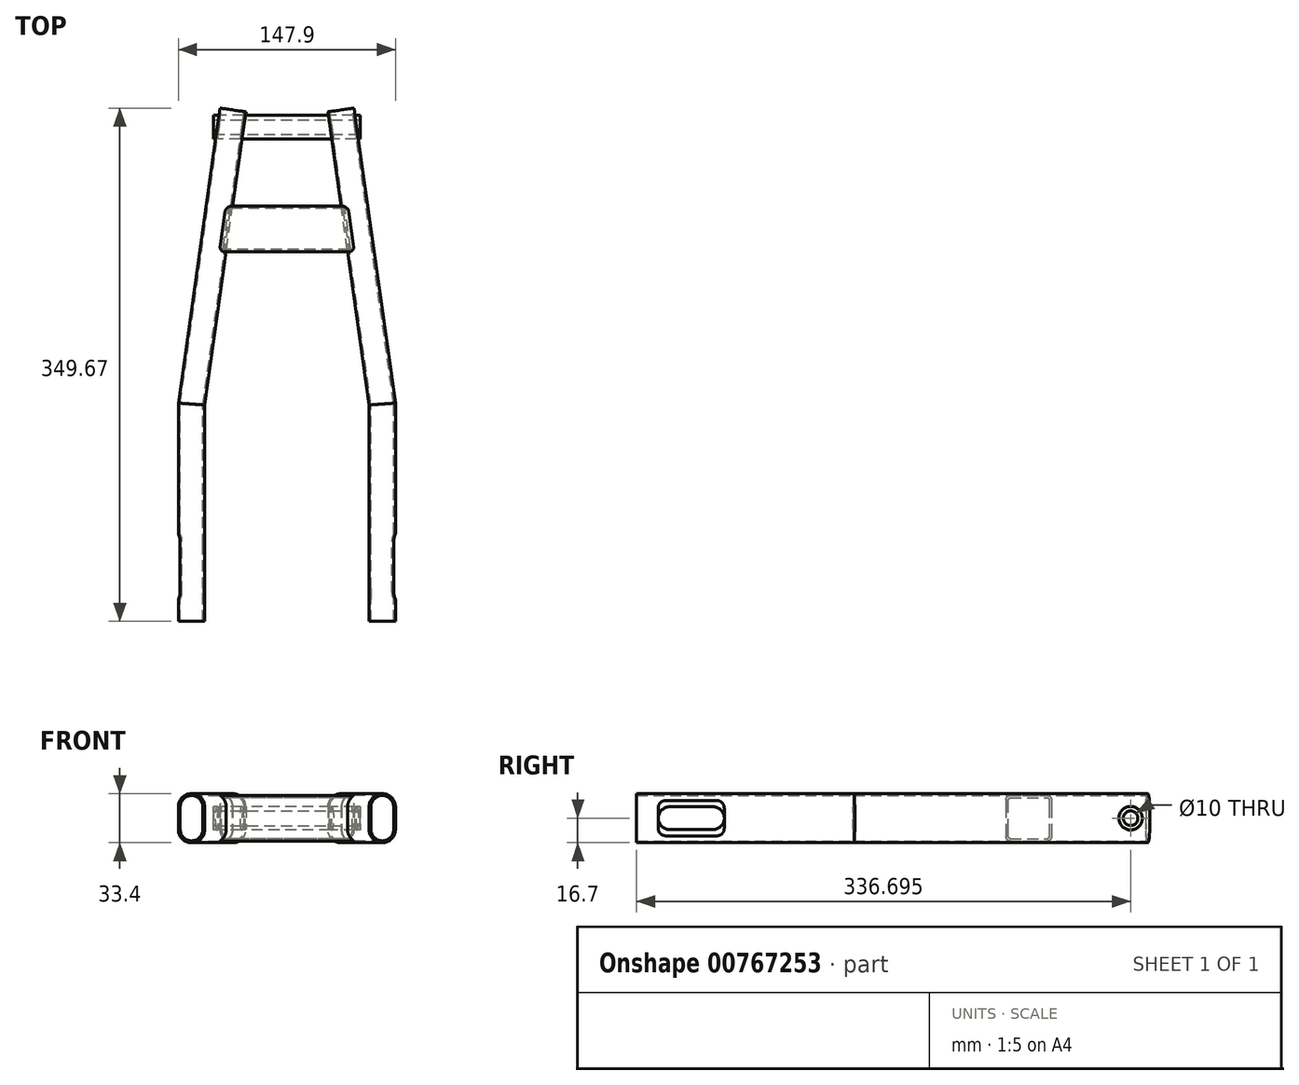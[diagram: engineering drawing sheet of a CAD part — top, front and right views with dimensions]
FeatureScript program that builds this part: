
annotation { "Feature Type Name" : "Feature", "Feature Type Description" : "" }
export const myFeature = defineFeature(function(context is Context, id is Id, definition is map)
    precondition{}
    {
        {
            var Q0;
            Q0=qCreatedBy(makeId("Top.planeOp"),FACE);
            var sketch = newSketch(context, id + "F0", { "sketchPlane" : qUnion([Q0])});
            skLineSegment(sketch, "E0", {"start": v(-65, 0) * mm, "end": v(-65, 148.03) * mm});
            skLineSegment(sketch, "E1", {"start": v(-65, 148.03) * mm, "end": v(-36.84, 348.42) * mm});
            skSolve(sketch);
        }
        {
            var Q0;
            Q0=qCreatedBy(makeId("Front.planeOp"),FACE);
            var sketch = newSketch(context, id + "F1", { "sketchPlane" : qUnion([Q0])});
            skLineSegment(sketch, "E2.left", {"start": v(-57.25, -7.75) * mm, "end": v(-57.25, 7.75) * mm});
            skLineSegment(sketch, "E2.right", {"start": v(-72.75, -7.75) * mm, "end": v(-72.75, 7.75) * mm});
            skPoint(sketch, "E2.middle", {"position": v(-65, 0) * mm});
            skArc(sketch, "E3", {"start": v(-57.25, 7.75) * mm, "mid": v(-65, 15.5) * mm, "end": v(-72.75, 7.75) * mm});
            skArc(sketch, "E4", {"start": v(-72.75, -7.75) * mm, "mid": v(-65, -15.5) * mm, "end": v(-57.25, -7.75) * mm});
            skCircle(sketch, "E5", {"center": v(-65, 0) * mm, "radius": 3 * mm});
            skLineSegment(sketch, "E6", {"start": v(-56.05, 7.75) * mm, "end": v(-56.05, -7.75) * mm});
            skLineSegment(sketch, "E7", {"start": v(-73.95, 7.75) * mm, "end": v(-73.95, -7.75) * mm});
            skArc(sketch, "E8", {"start": v(-56.05, 7.75) * mm, "mid": v(-65, 16.7) * mm, "end": v(-73.95, 7.75) * mm});
            skArc(sketch, "E9", {"start": v(-73.95, -7.75) * mm, "mid": v(-65, -16.7) * mm, "end": v(-56.05, -7.75) * mm});
            skSolve(sketch);
        }
        {
            var Q0;
            Q0 = qSketchRegion(id + "F1", true);
            var Q1;
            Q1=sQuery(id+"F0.wireOp",EDGE,"E0");
            var Q2;
            Q2=sQuery(id+"F0.wireOp",EDGE,"E1");
            sweep(context, id + "F2", {"profiles" : qUnion([Q0]), "path" : qUnion([Q1, Q2])});
        }
        {
            var Q0;
            Q0=makeQuery(id+"F2.opSweep","SWEPT_BODY",BODY,{"disambiguationData":[OSD([sQuery(id+"F0.wireOp",EDGE,"E1"),sQuery(id+"F1.wireOp",EDGE,"E2.left"),sQuery(id+"F1.wireOp",EDGE,"E2.right"),sQuery(id+"F1.wireOp",EDGE,"E3"),sQuery(id+"F1.wireOp",EDGE,"E4"),sQuery(id+"F1.wireOp",EDGE,"E6"),sQuery(id+"F1.wireOp",EDGE,"E7"),sQuery(id+"F1.wireOp",EDGE,"E8"),sQuery(id+"F1.wireOp",EDGE,"E9")])]});
            var Q1;
            Q1=qCreatedBy(makeId("Right.planeOp"),FACE);
            mirror(context, id + "F3", {"entities" : qUnion([Q0]), "mirrorPlane" : qUnion([Q1])});
        }
        {
            var Q0;
            Q0=makeQuery(id+"F3.opPattern","COPY",FACE,{"derivedFrom":makeQuery(id+"F2.opSweep","SWEPT_FACE",FACE,{"disambiguationData":[OSD([sQuery(id+"F0.wireOp",EDGE,"E0"),sQuery(id+"F1.wireOp",EDGE,"E7")])]}),"instanceName":"1"});
            cPlane(context, id + "F4", {"entities" : qUnion([Q0]), "cplaneType" : CPlaneType.OFFSET, "offset" : 25 * mm, "width" : 150 * mm, "height" : 150 * mm});
        }
        {
            var Q0;
            Q0=qCreatedBy(id+"F4.planeOp",FACE);
            var sketch = newSketch(context, id + "F5", { "sketchPlane" : qUnion([Q0])});
            skLineSegment(sketch, "E10.bottom", {"start": v(52.04, -7.75) * mm, "end": v(22.54, -7.75) * mm});
            skLineSegment(sketch, "E10.top", {"start": v(52.04, 7.75) * mm, "end": v(22.54, 7.75) * mm});
            skPoint(sketch, "E10.middle", {"position": v(37.3, 0) * mm});
            skArc(sketch, "E11", {"start": v(52.04, -7.75) * mm, "mid": v(59.8, 0) * mm, "end": v(52.04, 7.75) * mm});
            skArc(sketch, "E12", {"start": v(22.54, 7.75) * mm, "mid": v(14.8, 0) * mm, "end": v(22.54, -7.75) * mm});
            skLineSegment(sketch, "E13", {"start": v(52.04, 7.75) * mm, "end": v(52.04, -7.75) * mm});
            skSolve(sketch);
        }
        {
            var Q0;
            Q0 = qSketchRegion(id + "F5", true);
            extrude(context, id + "F6", {"entities" : qUnion([Q0]), "operationType" : NewBodyOperationType.REMOVE, "oppositeDirection" : true, "depth" : 222 * mm, "offsetDistance" : 25 * mm});
        }
        {
            var Q0;
            Q0=makeQuery(id+"F2.opSweep","SWEPT_FACE",FACE,{"disambiguationData":[OSD([sQuery(id+"F0.wireOp",EDGE,"E0"),sQuery(id+"F1.wireOp",EDGE,"E7")])]});
            var sketch = newSketch(context, id + "F7", { "sketchPlane" : qUnion([Q0])});
            skLineSegment(sketch, "E14.bottom", {"start": v(-22.54, -7.75) * mm, "end": v(-52.04, -7.75) * mm});
            skLineSegment(sketch, "E14.top", {"start": v(-22.54, 7.75) * mm, "end": v(-52.04, 7.75) * mm});
            skPoint(sketch, "E14.middle", {"position": v(-37.3, 0) * mm});
            skArc(sketch, "E15", {"start": v(-22.54, -7.75) * mm, "mid": v(-14.8, 0) * mm, "end": v(-22.54, 7.75) * mm});
            skArc(sketch, "E16", {"start": v(-52.04, 7.75) * mm, "mid": v(-59.8, 0) * mm, "end": v(-52.04, -7.75) * mm});
            skSolve(sketch);
        }
        {
            var Q0;
            Q0 = qSketchRegion(id + "F7", true);
            extrude(context, id + "F8", {"entities" : qUnion([Q0]), "operationType" : NewBodyOperationType.REMOVE, "oppositeDirection" : true, "depth" : 25 * mm, "offsetDistance" : 25 * mm});
        }
        {
            var Q0;
            Q0=qCreatedBy(id+"F4.planeOp",FACE);
            var sketch = newSketch(context, id + "F9", { "sketchPlane" : qUnion([Q0])});
            skLineSegment(sketch, "E17.bottom", {"start": v(54.76, -12) * mm, "end": v(19.76, -12) * mm});
            skLineSegment(sketch, "E17.top", {"start": v(54.76, 12) * mm, "end": v(19.76, 12) * mm});
            skLineSegment(sketch, "E17.left", {"start": v(59.76, -7) * mm, "end": v(59.76, 7) * mm});
            skLineSegment(sketch, "E17.right", {"start": v(14.76, -7) * mm, "end": v(14.76, 7) * mm});
            skPoint(sketch, "E17.middle", {"position": v(37.26, 0) * mm});
            skPoint(sketch, "E18.visualSharp", {"position": v(14.76, 12) * mm});
            skArc(sketch, "E18.filletArc", {"start": v(19.76, 12) * mm, "mid": v(16.22, 10.54) * mm, "end": v(14.76, 7) * mm});
            skPoint(sketch, "E19.visualSharp", {"position": v(59.76, 12) * mm});
            skArc(sketch, "E19.filletArc", {"start": v(59.76, 7) * mm, "mid": v(58.3, 10.54) * mm, "end": v(54.76, 12) * mm});
            skPoint(sketch, "E20.visualSharp", {"position": v(59.76, -12) * mm});
            skArc(sketch, "E20.filletArc", {"start": v(54.76, -12) * mm, "mid": v(58.3, -10.54) * mm, "end": v(59.76, -7) * mm});
            skPoint(sketch, "E21.visualSharp", {"position": v(14.76, -12) * mm});
            skArc(sketch, "E21.filletArc", {"start": v(14.76, -7) * mm, "mid": v(16.22, -10.54) * mm, "end": v(19.76, -12) * mm});
            skSolve(sketch);
        }
        {
            var Q0;
            Q0 = qSketchRegion(id + "F9", true);
            extrude(context, id + "F10", {"entities" : qUnion([Q0]), "operationType" : NewBodyOperationType.REMOVE, "oppositeDirection" : true, "depth" : 30 * mm, "offsetDistance" : 25 * mm});
        }
        {
            var Q0;
            {var subQ2=sQuery(id+"F1.wireOp",EDGE,"E7");var subQ4=sQuery(id+"F0.wireOp",EDGE,"E0");Q0=makeQuery(id+"F8.boolean.opBoolean","SPLIT",FACE,{"disambiguationData":[TD([makeQuery(id+"F8.opExtrude","SWEPT_FACE",FACE,{"disambiguationData":[OSD([sQuery(id+"F7.wireOp",EDGE,"E16")])]})])],"derivedFrom":makeQuery(id+"F2.opSweep","SWEPT_FACE",FACE,{"disambiguationData":[OSD([subQ4,subQ2])]})});}
            var sketch = newSketch(context, id + "F11", { "sketchPlane" : qUnion([Q0])});
            skLineSegment(sketch, "E22.bottom", {"start": v(-19.76, -12) * mm, "end": v(-54.76, -12) * mm});
            skLineSegment(sketch, "E22.top", {"start": v(-19.76, 12) * mm, "end": v(-54.76, 12) * mm});
            skLineSegment(sketch, "E22.left", {"start": v(-14.76, -7) * mm, "end": v(-14.76, 7) * mm});
            skLineSegment(sketch, "E22.right", {"start": v(-59.76, -7) * mm, "end": v(-59.76, 7) * mm});
            skPoint(sketch, "E22.middle", {"position": v(-37.26, 0) * mm});
            skPoint(sketch, "E23.visualSharp", {"position": v(-59.76, 12) * mm});
            skArc(sketch, "E23.filletArc", {"start": v(-54.76, 12) * mm, "mid": v(-58.3, 10.54) * mm, "end": v(-59.76, 7) * mm});
            skPoint(sketch, "E24.visualSharp", {"position": v(-14.76, 12) * mm});
            skArc(sketch, "E24.filletArc", {"start": v(-14.76, 7) * mm, "mid": v(-16.22, 10.54) * mm, "end": v(-19.76, 12) * mm});
            skPoint(sketch, "E25.visualSharp", {"position": v(-14.76, -12) * mm});
            skArc(sketch, "E25.filletArc", {"start": v(-19.76, -12) * mm, "mid": v(-16.22, -10.54) * mm, "end": v(-14.76, -7) * mm});
            skPoint(sketch, "E26.visualSharp", {"position": v(-59.76, -12) * mm});
            skArc(sketch, "E26.filletArc", {"start": v(-59.76, -7) * mm, "mid": v(-58.3, -10.54) * mm, "end": v(-54.76, -12) * mm});
            skSolve(sketch);
        }
        {
            var Q0;
            Q0 = qSketchRegion(id + "F11", true);
            extrude(context, id + "F12", {"entities" : qUnion([Q0]), "operationType" : NewBodyOperationType.REMOVE, "oppositeDirection" : true, "depth" : 4 * mm, "offsetDistance" : 25 * mm});
        }
        {
            var Q0;
            Q0=qCreatedBy(makeId("Right.planeOp"),FACE);
            var sketch = newSketch(context, id + "F13", { "sketchPlane" : qUnion([Q0])});
            skCircle(sketch, "E27", {"center": v(336.7, 0) * mm, "radius": 8 * mm});
            skSolve(sketch);
        }
        {
            var Q0;
            Q0=qCreatedBy(makeId("Right.planeOp"),FACE);
            var sketch = newSketch(context, id + "F14", { "sketchPlane" : qUnion([Q0])});
            skLineSegment(sketch, "E28.bottom", {"start": v(279.78, -15.5) * mm, "end": v(254.78, -15.5) * mm});
            skLineSegment(sketch, "E28.top", {"start": v(279.78, 15.5) * mm, "end": v(254.78, 15.5) * mm});
            skLineSegment(sketch, "E28.left", {"start": v(282.78, -12.5) * mm, "end": v(282.78, 12.5) * mm});
            skLineSegment(sketch, "E28.right", {"start": v(251.78, -12.5) * mm, "end": v(251.78, 12.5) * mm});
            skPoint(sketch, "E28.middle", {"position": v(267.28, 0) * mm});
            skPoint(sketch, "E29.visualSharp", {"position": v(251.78, 15.5) * mm});
            skArc(sketch, "E29.filletArc", {"start": v(254.78, 15.5) * mm, "mid": v(252.66, 14.62) * mm, "end": v(251.78, 12.5) * mm});
            skPoint(sketch, "E30.visualSharp", {"position": v(282.78, 15.5) * mm});
            skArc(sketch, "E30.filletArc", {"start": v(282.78, 12.5) * mm, "mid": v(281.9, 14.62) * mm, "end": v(279.78, 15.5) * mm});
            skPoint(sketch, "E31.visualSharp", {"position": v(282.78, -15.5) * mm});
            skArc(sketch, "E31.filletArc", {"start": v(279.78, -15.5) * mm, "mid": v(281.9, -14.62) * mm, "end": v(282.78, -12.5) * mm});
            skPoint(sketch, "E32.visualSharp", {"position": v(251.78, -15.5) * mm});
            skArc(sketch, "E32.filletArc", {"start": v(251.78, -12.5) * mm, "mid": v(252.66, -14.62) * mm, "end": v(254.78, -15.5) * mm});
            skLineSegment(sketch, "E33", {"start": v(253.38, 12.5) * mm, "end": v(253.38, -12.5) * mm});
            skLineSegment(sketch, "E34", {"start": v(254.78, -13.9) * mm, "end": v(279.78, -13.9) * mm});
            skLineSegment(sketch, "E35", {"start": v(281.18, -12.5) * mm, "end": v(281.18, 12.5) * mm});
            skLineSegment(sketch, "E36", {"start": v(279.78, 13.9) * mm, "end": v(254.78, 13.9) * mm});
            skPoint(sketch, "E37.orphan", {"position": v(253.38, 14.74) * mm});
            skPoint(sketch, "E38.visualSharp", {"position": v(253.38, 13.9) * mm});
            skArc(sketch, "E38.filletArc", {"start": v(254.78, 13.9) * mm, "mid": v(253.8, 13.49) * mm, "end": v(253.38, 12.5) * mm});
            skPoint(sketch, "E39.visualSharp", {"position": v(253.38, -13.9) * mm});
            skArc(sketch, "E39.filletArc", {"start": v(253.38, -12.5) * mm, "mid": v(253.8, -13.49) * mm, "end": v(254.78, -13.9) * mm});
            skPoint(sketch, "E40.visualSharp", {"position": v(281.18, -13.9) * mm});
            skArc(sketch, "E40.filletArc", {"start": v(279.78, -13.9) * mm, "mid": v(280.77, -13.49) * mm, "end": v(281.18, -12.5) * mm});
            skPoint(sketch, "E41.visualSharp", {"position": v(281.18, 13.9) * mm});
            skArc(sketch, "E41.filletArc", {"start": v(281.18, 12.5) * mm, "mid": v(280.77, 13.49) * mm, "end": v(279.78, 13.9) * mm});
            skSolve(sketch);
        }
        {
            var Q0;
            Q0 = qSketchRegion(id + "F14", true);
            var Q1;
            Q1=makeQuery(id+"F3.opPattern","COPY",BODY,{"derivedFrom":makeQuery(id+"F2.opSweep","SWEPT_BODY",BODY,{"disambiguationData":[OSD([sQuery(id+"F0.wireOp",EDGE,"E1"),sQuery(id+"F1.wireOp",EDGE,"E2.left"),sQuery(id+"F1.wireOp",EDGE,"E2.right"),sQuery(id+"F1.wireOp",EDGE,"E3"),sQuery(id+"F1.wireOp",EDGE,"E4"),sQuery(id+"F1.wireOp",EDGE,"E6"),sQuery(id+"F1.wireOp",EDGE,"E7"),sQuery(id+"F1.wireOp",EDGE,"E8"),sQuery(id+"F1.wireOp",EDGE,"E9")])]}),"instanceName":"1"});
            extrude(context, id + "F15", {"entities" : qUnion([Q0]), "operationType" : NewBodyOperationType.ADD, "endBound" : BoundingType.UP_TO_BODY, "depth" : 25 * mm, "endBoundEntityBody" : qUnion([Q1]), "offsetDistance" : 25 * mm});
        }
        {
            var Q0;
            Q0=makeQuery(id+"F3.opPattern","COPY",BODY,{"derivedFrom":makeQuery(id+"F2.opSweep","SWEPT_BODY",BODY,{"disambiguationData":[OSD([sQuery(id+"F0.wireOp",EDGE,"E1"),sQuery(id+"F1.wireOp",EDGE,"E2.left"),sQuery(id+"F1.wireOp",EDGE,"E2.right"),sQuery(id+"F1.wireOp",EDGE,"E3"),sQuery(id+"F1.wireOp",EDGE,"E4"),sQuery(id+"F1.wireOp",EDGE,"E6"),sQuery(id+"F1.wireOp",EDGE,"E7"),sQuery(id+"F1.wireOp",EDGE,"E8"),sQuery(id+"F1.wireOp",EDGE,"E9")])]}),"instanceName":"1"});
            var Q1;
            Q1=qCreatedBy(makeId("Right.planeOp"),FACE);
            mirror(context, id + "F16", {"entities" : qUnion([Q0]), "mirrorPlane" : qUnion([Q1])});
        }
        {
            var Q0;
            Q0=makeQuery(id+"F13.imprint","IMPRINT",FACE,{"disambiguationData":[TD([[makeQuery(id+"F13.imprint","IMPRINT",EDGE,{"derivedFrom":sQuery(id+"F13.wireOp",EDGE,"E27")}),1.0]])]});
            var Q1;
            Q1=makeQuery(id+"F3.opPattern","COPY",BODY,{"derivedFrom":makeQuery(id+"F2.opSweep","SWEPT_BODY",BODY,{"disambiguationData":[OSD([sQuery(id+"F0.wireOp",EDGE,"E1"),sQuery(id+"F1.wireOp",EDGE,"E2.left"),sQuery(id+"F1.wireOp",EDGE,"E2.right"),sQuery(id+"F1.wireOp",EDGE,"E3"),sQuery(id+"F1.wireOp",EDGE,"E4"),sQuery(id+"F1.wireOp",EDGE,"E6"),sQuery(id+"F1.wireOp",EDGE,"E7"),sQuery(id+"F1.wireOp",EDGE,"E8"),sQuery(id+"F1.wireOp",EDGE,"E9")])]}),"instanceName":"1"});
            extrude(context, id + "F17", {"entities" : qUnion([Q0]), "operationType" : NewBodyOperationType.ADD, "endBound" : BoundingType.SYMMETRIC, "depth" : 100 * mm, "endBoundEntityBody" : qUnion([Q1]), "offsetDistance" : 25 * mm});
        }
        {
            var Q0;
            Q0=makeQuery(id+"F17.opExtrude","CAP_FACE",FACE,{"disambiguationData":[OSD([sQuery(id+"F13.wireOp",EDGE,"E27")])],"isStart":false});
            var sketch = newSketch(context, id + "F18", { "sketchPlane" : qUnion([Q0])});
            skCircle(sketch, "E42", {"center": v(336.7, 0) * mm, "radius": 5 * mm});
            skSolve(sketch);
        }
        {
            var Q0;
            Q0 = qSketchRegion(id + "F18", true);
            extrude(context, id + "F19", {"entities" : qUnion([Q0]), "operationType" : NewBodyOperationType.REMOVE, "oppositeDirection" : true, "depth" : 110 * mm, "offsetDistance" : 25 * mm});
        }
    });
